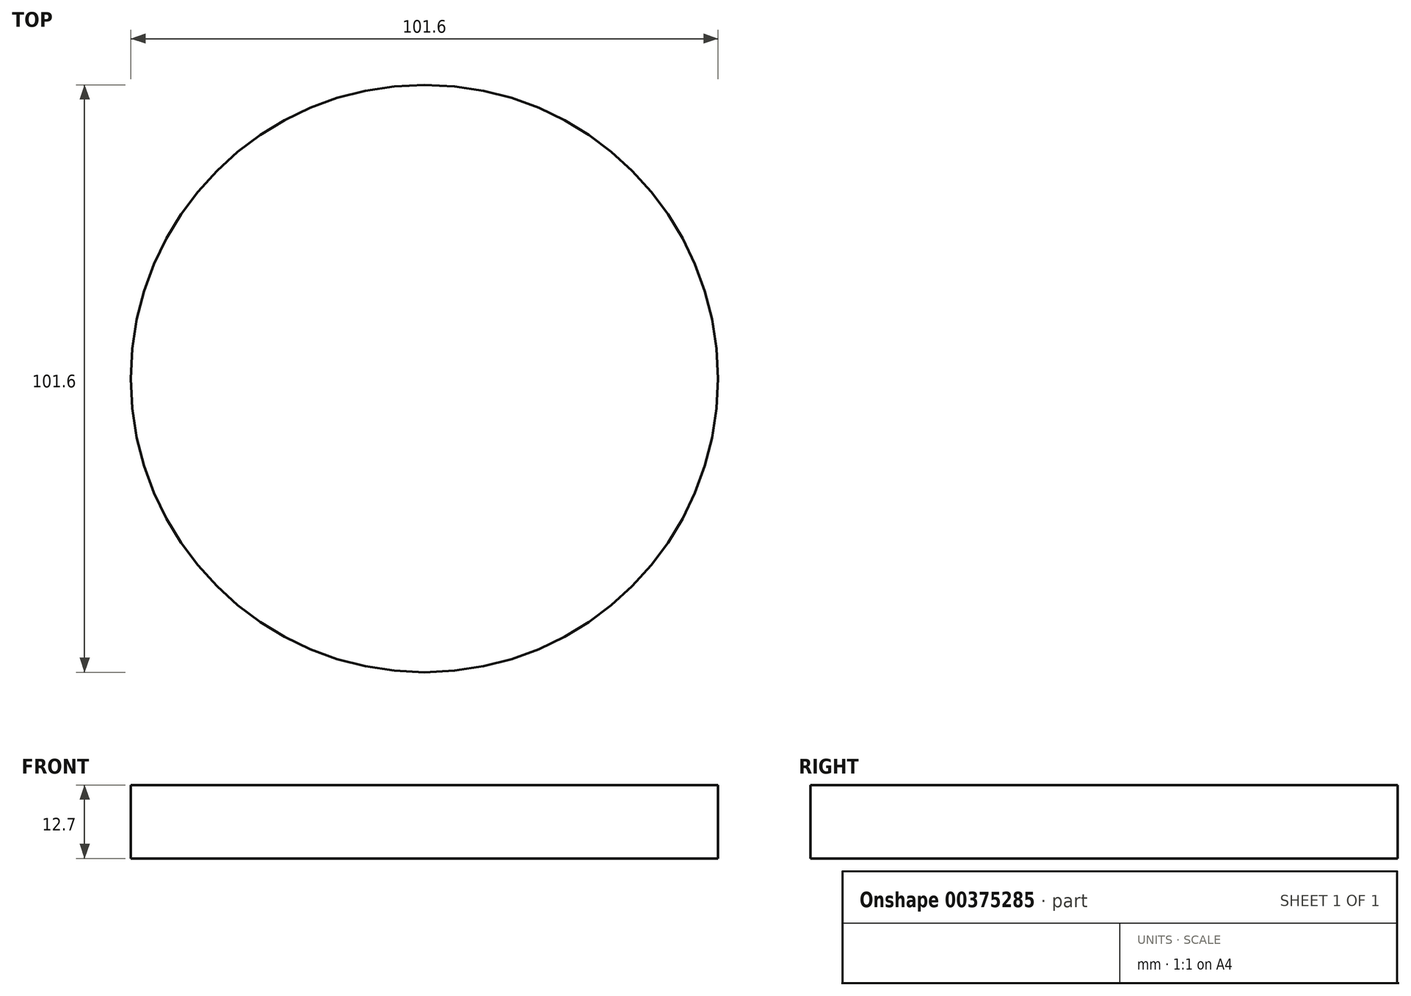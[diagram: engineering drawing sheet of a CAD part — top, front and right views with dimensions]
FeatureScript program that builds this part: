
annotation { "Feature Type Name" : "Feature", "Feature Type Description" : "" }
export const myFeature = defineFeature(function(context is Context, id is Id, definition is map)
    precondition{}
    {
        {
            var Q0;
            Q0=qCreatedBy(makeId("Top.planeOp"),FACE);
            var sketch = newSketch(context, id + "F0", { "sketchPlane" : qUnion([Q0])});
            skCircle(sketch, "E0", {"center": v(0, 0) * mm, "radius": 50.8 * mm});
            skSolve(sketch);
        }
        {
            var Q0;
            Q0 = qSketchRegion(id + "F0", true);
            extrude(context, id + "F1", {"entities" : qUnion([Q0]), "depth" : 12.7 * mm});
        }
    });
